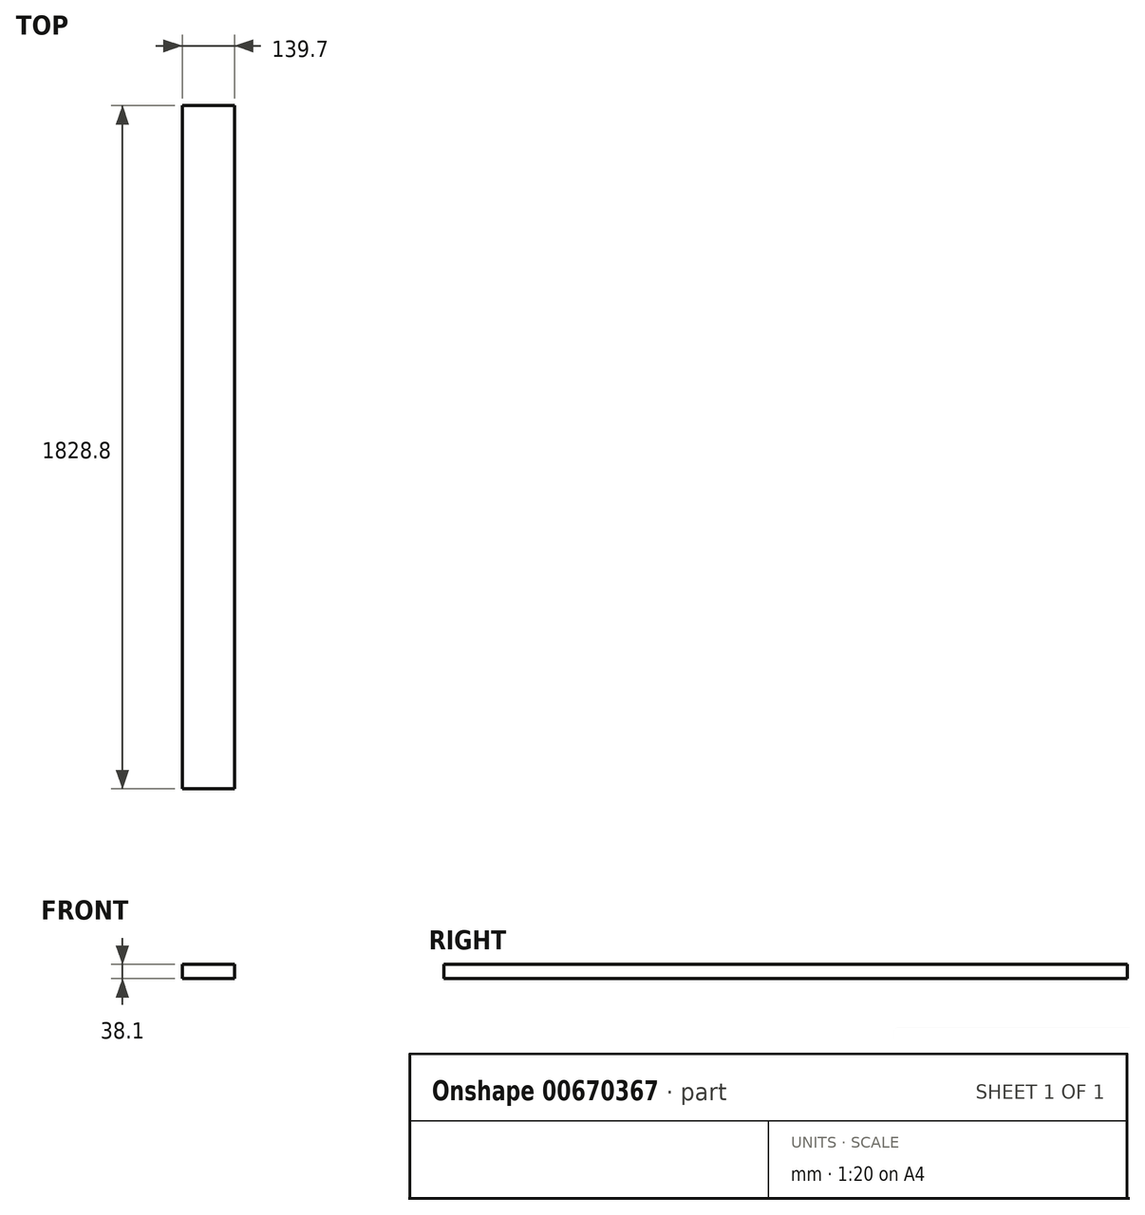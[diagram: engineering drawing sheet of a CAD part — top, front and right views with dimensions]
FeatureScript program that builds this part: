
annotation { "Feature Type Name" : "Feature", "Feature Type Description" : "" }
export const myFeature = defineFeature(function(context is Context, id is Id, definition is map)
    precondition{}
    {
        {
            var Q0;
            Q0=qCreatedBy(makeId("Front.planeOp"),FACE);
            var sketch = newSketch(context, id + "F0", { "sketchPlane" : qUnion([Q0])});
            skLineSegment(sketch, "E0.bottom", {"start": v(-44.45, 19.05) * mm, "end": v(95.25, 19.05) * mm});
            skLineSegment(sketch, "E0.top", {"start": v(-44.45, -19.05) * mm, "end": v(95.25, -19.05) * mm});
            skLineSegment(sketch, "E0.left", {"start": v(-44.45, 19.05) * mm, "end": v(-44.45, -19.05) * mm});
            skLineSegment(sketch, "E0.right", {"start": v(95.25, 19.05) * mm, "end": v(95.25, -19.05) * mm});
            skSolve(sketch);
        }
        {
            var Q0;
            Q0=makeQuery(id+"F0.imprint","IMPRINT",FACE,{"disambiguationData":[TD([[makeQuery(id+"F0.imprint","IMPRINT",EDGE,{"derivedFrom":sQuery(id+"F0.wireOp",EDGE,"E0.bottom")}),-1.0]])]});
            extrude(context, id + "F1", {"entities" : qUnion([Q0]), "oppositeDirection" : true, "depth" : 1828.8 * mm, "offsetDistance" : 25.4 * mm});
        }
    });
